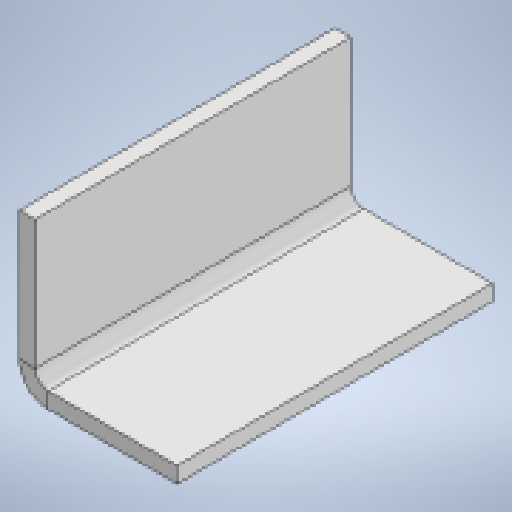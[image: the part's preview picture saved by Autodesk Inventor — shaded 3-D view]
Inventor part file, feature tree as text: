
AUTODESK INVENTOR PART (.ipt)
format: ipt  version: 2025 (Build 290162010, 162A)  size: 183,296 bytes
history: native  units: mm
features: sheet_metal_op x4, other x3, sketch x2
ambient origin geometry x8: Origin, YZ Plane, XZ Plane, XY Plane, X Axis, Y Axis, Z Axis, Center Point
bodies: Body1 (feature_tree)
feature tree (9):
  sheet_metal_op  "Face2"
  sheet_metal_op  "Flange2"
  sketch  "Sketch6"  dims[d46=6.0mm]
  other  "Plate3"
  sketch  "Sketch7"  dims[d47=60.0mm d48=120.0mm d49=6.0mm d50=3.0mm d51=12.0mm d52=5.0mm d53=60.0mm d54=90.0deg d55=5.0mm d56=24.0mm d57=6.0mm d58=5.0mm]
  other  "Plate4"
  sheet_metal_op  "Bend2"
  sheet_metal_op  "Corner2"
  other  "Definition1"
